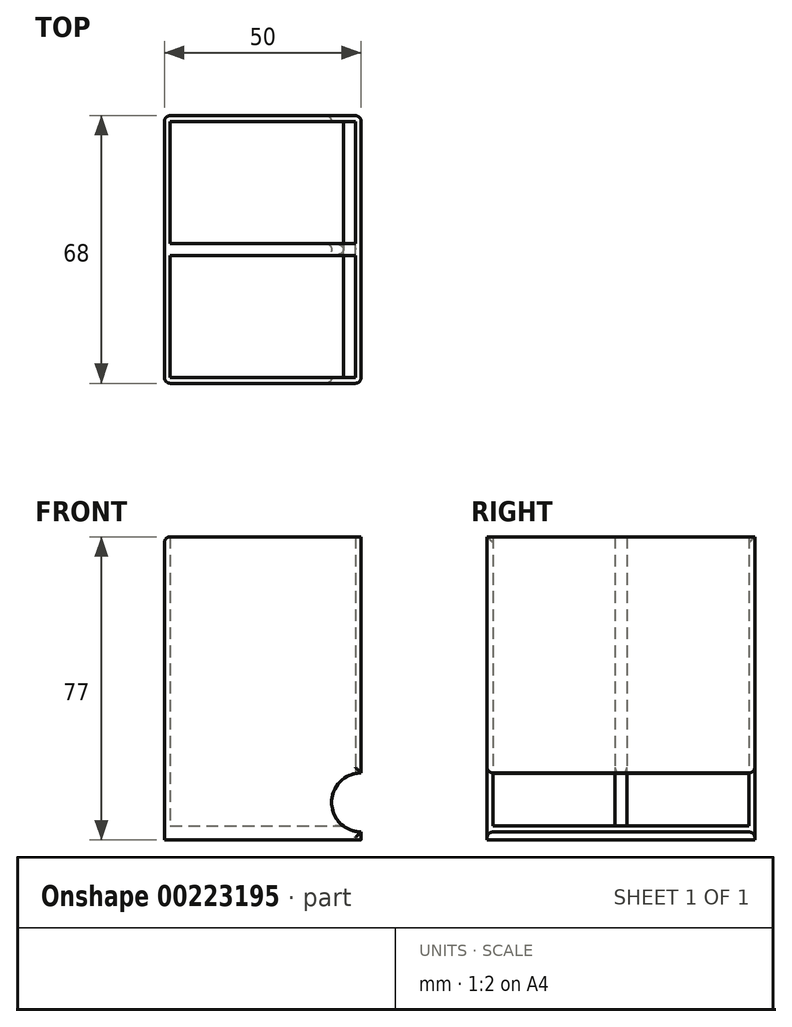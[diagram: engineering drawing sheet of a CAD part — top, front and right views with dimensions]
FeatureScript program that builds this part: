
annotation { "Feature Type Name" : "Feature", "Feature Type Description" : "" }
export const myFeature = defineFeature(function(context is Context, id is Id, definition is map)
    precondition{}
    {
        {
            var Q0;
            Q0=qCreatedBy(makeId("Front.planeOp"),FACE);
            var sketch = newSketch(context, id + "F0", { "sketchPlane" : qUnion([Q0])});
            skLineSegment(sketch, "E0.bottom", {"start": v(-50, 75) * mm, "end": v(0, 75) * mm});
            skLineSegment(sketch, "E0.top", {"start": v(-50, 0) * mm, "end": v(0, 0) * mm});
            skLineSegment(sketch, "E0.left", {"start": v(-50, 75) * mm, "end": v(-50, 0) * mm});
            skLineSegment(sketch, "E0.right", {"start": v(0, 75) * mm, "end": v(0, 0) * mm});
            skArc(sketch, "E1", {"start": v(0, 15) * mm, "mid": v(-7.5, 7.5) * mm, "end": v(0, 0) * mm});
            skSolve(sketch);
        }
        {
            var Q0;
            {var subQ1=sQuery(id+"F0.wireOp",EDGE,"E0.bottom");Q0=makeQuery(id+"F0.imprint","IMPRINT",FACE,{"disambiguationData":[TD([[makeQuery(id+"F0.imprint","IMPRINT",EDGE,{"derivedFrom":subQ1}),-1.0]])]});}
            extrude(context, id + "F1", {"entities" : qUnion([Q0]), "depth" : 34 * mm});
        }
        {
            var Q0;
            Q0=makeQuery(id+"F1.opExtrude","SWEPT_FACE",FACE,{"disambiguationData":[OSD([sQuery(id+"F0.wireOp",EDGE,"E0.bottom")])]});
            var Q1;
            Q1=makeQuery(id+"F1.opExtrude","SWEPT_FACE",FACE,{"disambiguationData":[OSD([sQuery(id+"F0.wireOp",EDGE,"E1")])]});
            shell(context, id + "F2", {"entities" : qUnion([Q0, Q1]), "thickness" : 1.5 * mm});
        }
        {
            var Q0;
            Q0=makeQuery(id+"F1.opExtrude","SWEPT_FACE",FACE,{"disambiguationData":[OSD([sQuery(id+"F0.wireOp",EDGE,"E0.top")])]});
            extrude(context, id + "F3", {"entities" : qUnion([Q0]), "operationType" : NewBodyOperationType.ADD, "depth" : 2 * mm});
        }
        {
            var Q0;
            Q0=makeQuery(id+"F1.opExtrude","SWEPT_BODY",BODY,{"disambiguationData":[OSD([sQuery(id+"F0.wireOp",EDGE,"E0.bottom"),sQuery(id+"F0.wireOp",EDGE,"E0.top"),sQuery(id+"F0.wireOp",EDGE,"E0.left"),sQuery(id+"F0.wireOp",EDGE,"E0.right"),sQuery(id+"F0.wireOp",EDGE,"E1")])]});
            var Q1;
            {var subQ0=sQuery(id+"F0.wireOp",EDGE,"E0.top");Q1=makeQuery(id+"F3.boolean.opBoolean","MERGE",FACE,{"derivedFrom":[makeQuery(id+"F1.opExtrude","CAP_FACE",FACE,{"disambiguationData":[OSD([sQuery(id+"F0.wireOp",EDGE,"E0.bottom"),subQ0,sQuery(id+"F0.wireOp",EDGE,"E0.left"),sQuery(id+"F0.wireOp",EDGE,"E0.right"),sQuery(id+"F0.wireOp",EDGE,"E1")])],"isStart":true}),makeQuery(id+"F3.opExtrude","SWEPT_FACE",FACE,{"disambiguationData":[OSD([subQ0]),TDD([makeQuery(id+"F1.opExtrude","CAP_EDGE",EDGE,{"disambiguationData":[OSD([subQ0])],"isStart":true})])]})]});}
            mirror(context, id + "F4", {"entities" : qUnion([Q0]), "mirrorPlane" : qUnion([Q1])});
        }
        {
            var Q0;
            Q0=makeQuery(id+"F1.opExtrude","SWEPT_BODY",BODY,{"disambiguationData":[OSD([sQuery(id+"F0.wireOp",EDGE,"E0.bottom"),sQuery(id+"F0.wireOp",EDGE,"E0.top"),sQuery(id+"F0.wireOp",EDGE,"E0.left"),sQuery(id+"F0.wireOp",EDGE,"E0.right"),sQuery(id+"F0.wireOp",EDGE,"E1")])]});
            var Q1;
            Q1=makeQuery(id+"F4.opPattern","COPY",BODY,{"derivedFrom":makeQuery(id+"F1.opExtrude","SWEPT_BODY",BODY,{"disambiguationData":[OSD([sQuery(id+"F0.wireOp",EDGE,"E0.bottom"),sQuery(id+"F0.wireOp",EDGE,"E0.top"),sQuery(id+"F0.wireOp",EDGE,"E0.left"),sQuery(id+"F0.wireOp",EDGE,"E0.right"),sQuery(id+"F0.wireOp",EDGE,"E1")])]}),"instanceName":"1"});
            booleanBodies(context, id + "F5", {"operationType" : BooleanOperationType.UNION, "tools" : qUnion([Q0, Q1])});
        }
        {
            var Q0;
            Q0=makeQuery(id+"F1.opExtrude","CAP_EDGE",EDGE,{"disambiguationData":[OSD([sQuery(id+"F0.wireOp",EDGE,"E0.right")])],"isStart":false});
            var Q1;
            {var subQ0=sQuery(id+"F0.wireOp",EDGE,"E0.left");var subQ1=sQuery(id+"F0.wireOp",EDGE,"E0.top");Q1=makeQuery(id+"F3.boolean.opBoolean","MERGE",EDGE,{"derivedFrom":[makeQuery(id+"F1.opExtrude","CAP_EDGE",EDGE,{"disambiguationData":[OSD([subQ0])],"isStart":false}),makeQuery(id+"F3.opExtrude","SWEPT_EDGE",EDGE,{"disambiguationData":[OSD([subQ1,subQ0]),TDD([makeQuery(id+"F1.opExtrude","CAP_VERTEX",VERTEX,{"disambiguationData":[OSD([subQ1,subQ0])],"isStart":false})])]})]});}
            var Q2;
            {var subQ0=sQuery(id+"F0.wireOp",EDGE,"E0.left");var subQ1=sQuery(id+"F0.wireOp",EDGE,"E0.top");Q2=makeQuery(id+"F4.opPattern","COPY",EDGE,{"derivedFrom":makeQuery(id+"F3.boolean.opBoolean","MERGE",EDGE,{"derivedFrom":[makeQuery(id+"F1.opExtrude","CAP_EDGE",EDGE,{"disambiguationData":[OSD([subQ0])],"isStart":false}),makeQuery(id+"F3.opExtrude","SWEPT_EDGE",EDGE,{"disambiguationData":[OSD([subQ1,subQ0]),TDD([makeQuery(id+"F1.opExtrude","CAP_VERTEX",VERTEX,{"disambiguationData":[OSD([subQ1,subQ0])],"isStart":false})])]})]}),"instanceName":"1"});}
            var Q3;
            {var subQ0=sQuery(id+"F0.wireOp",EDGE,"E1");var subQ1=sQuery(id+"F0.wireOp",EDGE,"E0.right");var subQ2=sQuery(id+"F0.wireOp",EDGE,"E0.top");Q3=makeQuery(id+"F4.opPattern","COPY",EDGE,{"derivedFrom":makeQuery(id+"F3.opExtrude","SWEPT_EDGE",EDGE,{"disambiguationData":[OSD([subQ2,subQ1,subQ0]),TDD([makeQuery(id+"F1.opExtrude","CAP_VERTEX",VERTEX,{"disambiguationData":[OSD([subQ2,subQ1,subQ0])],"isStart":false})])]}),"instanceName":"1"});}
            var Q4;
            {var subQ0=sQuery(id+"F0.wireOp",EDGE,"E1");var subQ1=sQuery(id+"F0.wireOp",EDGE,"E0.right");var subQ2=sQuery(id+"F0.wireOp",EDGE,"E0.top");Q4=makeQuery(id+"F3.opExtrude","SWEPT_EDGE",EDGE,{"disambiguationData":[OSD([subQ2,subQ1,subQ0]),TDD([makeQuery(id+"F1.opExtrude","CAP_VERTEX",VERTEX,{"disambiguationData":[OSD([subQ2,subQ1,subQ0])],"isStart":false})])]});}
            var Q5;
            {var subQ0=makeQuery(id+"F1.opExtrude","SWEPT_EDGE",EDGE,{"disambiguationData":[OSD([sQuery(id+"F0.wireOp",EDGE,"E0.bottom"),sQuery(id+"F0.wireOp",EDGE,"E0.left")])]});Q5=makeQuery(id+"F5.opBoolean","MERGE",EDGE,{"derivedFrom":[subQ0,makeQuery(id+"F4.opPattern","COPY",EDGE,{"derivedFrom":subQ0,"instanceName":"1"})]});}
            var Q6;
            Q6=makeQuery(id+"F4.opPattern","COPY",EDGE,{"derivedFrom":makeQuery(id+"F1.opExtrude","CAP_EDGE",EDGE,{"disambiguationData":[OSD([sQuery(id+"F0.wireOp",EDGE,"E0.right")])],"isStart":false}),"instanceName":"1"});
            var Q7;
            Q7=makeQuery(id+"F4.opPattern","COPY",EDGE,{"derivedFrom":makeQuery(id+"F1.opExtrude","CAP_EDGE",EDGE,{"disambiguationData":[OSD([sQuery(id+"F0.wireOp",EDGE,"E1")])],"isStart":false}),"instanceName":"1"});
            var Q8;
            {var subQ0=sQuery(id+"F0.wireOp",EDGE,"E1");Q8=makeQuery(id+"F4.opPattern","COPY",EDGE,{"derivedFrom":makeQuery(id+"F2.opShell","OFFSET_EDGE",EDGE,{"disambiguationData":[OSD([subQ0]),TDD([makeQuery(id+"F1.opExtrude","CAP_EDGE",EDGE,{"disambiguationData":[OSD([subQ0])],"isStart":true})])]}),"instanceName":"1"});}
            var Q9;
            {var subQ0=sQuery(id+"F0.wireOp",EDGE,"E1");Q9=makeQuery(id+"F2.opShell","OFFSET_EDGE",EDGE,{"disambiguationData":[OSD([subQ0]),TDD([makeQuery(id+"F1.opExtrude","CAP_EDGE",EDGE,{"disambiguationData":[OSD([subQ0])],"isStart":true})])]});}
            var Q10;
            Q10=makeQuery(id+"F1.opExtrude","CAP_EDGE",EDGE,{"disambiguationData":[OSD([sQuery(id+"F0.wireOp",EDGE,"E1")])],"isStart":false});
            fillet(context, id + "F6", {"entities" : qUnion([Q0, Q1, Q2, Q3, Q4, Q5, Q6, Q7, Q8, Q9, Q10]), "radius" : 1.5 * mm, "tangentPropagation" : true, "allowEdgeOverflow" : false});
        }
    });
